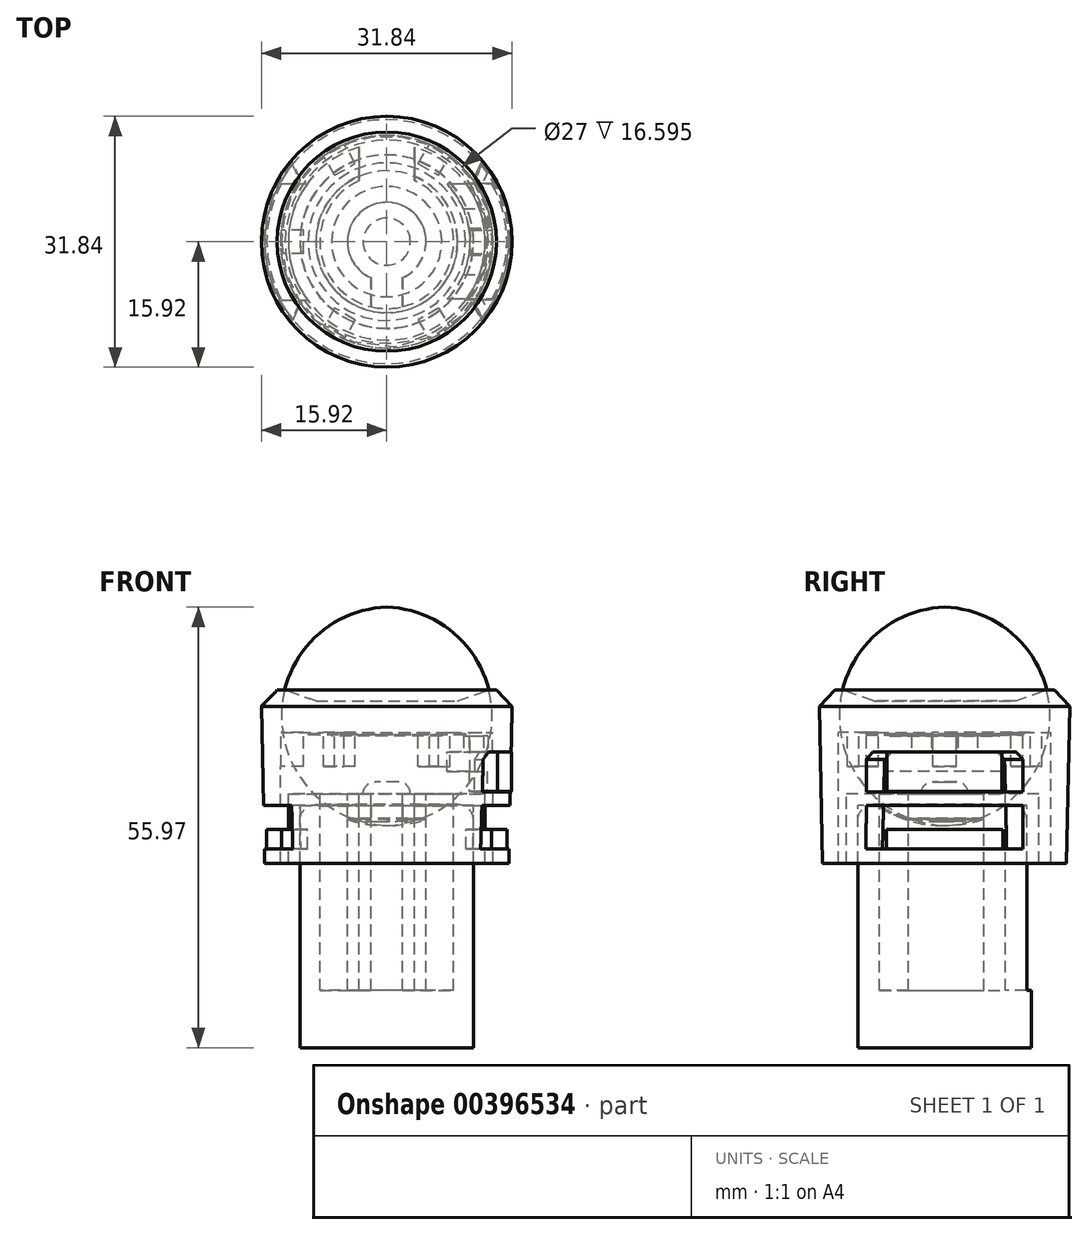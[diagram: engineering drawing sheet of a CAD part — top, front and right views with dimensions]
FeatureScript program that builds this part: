
annotation { "Feature Type Name" : "Feature", "Feature Type Description" : "" }
export const myFeature = defineFeature(function(context is Context, id is Id, definition is map)
    precondition{}
    {
        {
            var Q0;
            Q0=qCreatedBy(makeId("Front.planeOp"),FACE);
            var sketch = newSketch(context, id + "F0", { "sketchPlane" : qUnion([Q0])});
            skLineSegment(sketch, "E0", {"start": v(0, -0.44) * mm, "end": v(12.5, -0.44) * mm});
            skLineSegment(sketch, "E1", {"start": v(12.5, -0.44) * mm, "end": v(12.5, -9.24) * mm});
            skLineSegment(sketch, "E2", {"start": v(12.5, -9.24) * mm, "end": v(11, -9.24) * mm});
            skLineSegment(sketch, "E3", {"start": v(11, -9.24) * mm, "end": v(11, -1.94) * mm});
            skLineSegment(sketch, "E4", {"start": v(11, -1.94) * mm, "end": v(8.5, -1.94) * mm});
            skLineSegment(sketch, "E5.trimOffspring", {"start": v(0, -0.44) * mm, "end": v(0, -3.94) * mm, "construction": true});
            skLineSegment(sketch, "E6", {"start": v(0, -0.44) * mm, "end": v(0, -3.94) * mm});
            skPoint(sketch, "E7.start.orphan", {"position": v(0, 38.98) * mm});
            skFitSpline(sketch, "E8", {"points": [v(8.5, -1.94) * mm, v(4.82, -3.6) * mm, v(0, -3.94) * mm], "startDerivative": vector(-6.37, -4.3) * mm, "endDerivative": vector(-9.55, 0.19) * mm});
            skSolve(sketch);
        }
        {
            var Q0;
            Q0=qCreatedBy(makeId("Front.planeOp"),FACE);
            var sketch = newSketch(context, id + "F1", { "sketchPlane" : qUnion([Q0])});
            skLineSegment(sketch, "E9", {"start": v(0, 3.78) * mm, "end": v(0, -25.53) * mm, "construction": true});
            skLineSegment(sketch, "E10", {"start": v(11.03, -1.82) * mm, "end": v(11.03, -32.69) * mm});
            skLineSegment(sketch, "E11", {"start": v(11.03, -1.82) * mm, "end": v(8.62, -1.82) * mm});
            skLineSegment(sketch, "E12", {"start": v(0, -4.45) * mm, "end": v(0, -32.69) * mm});
            skArc(sketch, "E13", {"start": v(0, -4.45) * mm, "mid": v(4.53, -3.85) * mm, "end": v(8.62, -1.82) * mm});
            skLineSegment(sketch, "E14", {"start": v(0, -32.69) * mm, "end": v(11.03, -32.69) * mm});
            skSolve(sketch);
        }
        {
            var Q0;
            Q0=makeQuery(id+"F1.imprint","IMPRINT",FACE,{"disambiguationData":[TD([[makeQuery(id+"F1.imprint","IMPRINT",EDGE,{"derivedFrom":sQuery(id+"F1.wireOp",EDGE,"E10")}),-1.0]])]});
            var Q1;
            Q1=sQuery(id+"F1.wireOp",EDGE,"E12");
            revolve(context, id + "F2", {"entities" : qUnion([Q0]), "axis" : qUnion([Q1]), "revolveType" : RevolveType.FULL});
        }
        {
            var Q0;
            Q0=makeQuery(id+"F2.opRevolve","SWEPT_EDGE",EDGE,{"disambiguationData":[OSD([sQuery(id+"F1.wireOp",EDGE,"E10"),sQuery(id+"F1.wireOp",EDGE,"E11")])]});
            fillet(context, id + "F3", {"entities" : qUnion([Q0]), "radius" : 2 * mm, "tangentPropagation" : true, "allowEdgeOverflow" : false});
        }
        {
            var Q0;
            Q0=makeQuery(id+"F2.opRevolve","SWEPT_EDGE",EDGE,{"disambiguationData":[OSD([sQuery(id+"F1.wireOp",EDGE,"E11"),sQuery(id+"F1.wireOp",EDGE,"E13")])]});
            fillet(context, id + "F4", {"entities" : qUnion([Q0]), "radius" : 2 * mm, "tangentPropagation" : true, "allowEdgeOverflow" : false});
        }
        {
            var Q0;
            Q0 = qSketchRegion(id + "F0", true);
            var Q1;
            Q1=sQuery(id+"F0.wireOp",EDGE,"E6");
            revolve(context, id + "F5", {"entities" : qUnion([Q0]), "axis" : qUnion([Q1]), "revolveType" : RevolveType.FULL});
        }
        {
            var Q0;
            Q0=makeQuery(id+"F5.opRevolve","SWEPT_FACE",FACE,{"disambiguationData":[OSD([sQuery(id+"F0.wireOp",EDGE,"E0")])]});
            var sketch = newSketch(context, id + "F6", { "sketchPlane" : qUnion([Q0])});
            skArc(sketch, "E15", {"start": v(2, -4.58) * mm, "mid": v(0, 5) * mm, "end": v(-2, -4.58) * mm});
            skArc(sketch, "E16", {"start": v(2, -8.26) * mm, "mid": v(0, 8.5) * mm, "end": v(-2, -8.26) * mm});
            skLineSegment(sketch, "E17", {"start": v(0, 12.95) * mm, "end": v(0, -13.26) * mm, "construction": true});
            skLineSegment(sketch, "E18", {"start": v(2, -4.58) * mm, "end": v(2, -8.26) * mm});
            skLineSegment(sketch, "E19", {"start": v(-2, -4.58) * mm, "end": v(-2, -8.26) * mm});
            skSolve(sketch);
        }
        {
            var Q0;
            Q0=makeQuery(id+"F6.imprint","IMPRINT",FACE,{"disambiguationData":[TD([[makeQuery(id+"F6.imprint","IMPRINT",EDGE,{"derivedFrom":sQuery(id+"F6.wireOp",EDGE,"E15")}),-1.0]])]});
            extrude(context, id + "F7", {"entities" : qUnion([Q0]), "operationType" : NewBodyOperationType.REMOVE, "oppositeDirection" : true, "depth" : 25 * mm});
        }
        {
            var Q0;
            Q0=makeQuery(id+"F5.opRevolve","SWEPT_FACE",FACE,{"disambiguationData":[OSD([sQuery(id+"F0.wireOp",EDGE,"E0")])]});
            var sketch = newSketch(context, id + "F8", { "sketchPlane" : qUnion([Q0])});
            skLineSegment(sketch, "E20", {"start": v(0, 27.7) * mm, "end": v(0, -25.88) * mm, "construction": true});
            skLineSegment(sketch, "E21.bottom", {"start": v(-3.5, 14) * mm, "end": v(3.5, 14) * mm});
            skLineSegment(sketch, "E21.top", {"start": v(-3.5, 6.54) * mm, "end": v(3.5, 6.54) * mm});
            skLineSegment(sketch, "E21.left", {"start": v(-3.5, 14) * mm, "end": v(-3.5, 6.54) * mm});
            skLineSegment(sketch, "E21.right", {"start": v(3.5, 14) * mm, "end": v(3.5, 6.54) * mm});
            skSolve(sketch);
        }
        {
            var Q0;
            Q0 = qSketchRegion(id + "F8", true);
            extrude(context, id + "F9", {"entities" : qUnion([Q0]), "operationType" : NewBodyOperationType.REMOVE, "oppositeDirection" : true, "depth" : 25 * mm});
        }
        {
            var Q0;
            Q0=makeQuery(id+"F5.opRevolve","SWEPT_FACE",FACE,{"disambiguationData":[OSD([sQuery(id+"F0.wireOp",EDGE,"E0")])]});
            var sketch = newSketch(context, id + "F10", { "sketchPlane" : qUnion([Q0])});
            skCircle(sketch, "E22", {"center": v(0, 0) * mm, "radius": 3 * mm});
            skSolve(sketch);
        }
        {
            var Q0;
            Q0 = qSketchRegion(id + "F10", true);
            extrude(context, id + "F11", {"entities" : qUnion([Q0]), "operationType" : NewBodyOperationType.ADD, "depth" : 1.5 * mm});
        }
        {
            var Q0;
            Q0=makeQuery(id+"F11.opExtrude","CAP_EDGE",EDGE,{"disambiguationData":[OSD([sQuery(id+"F10.wireOp",EDGE,"E22")])],"isStart":false});
            fillet(context, id + "F12", {"entities" : qUnion([Q0]), "radius" : 1.5 * mm, "tangentPropagation" : true, "allowEdgeOverflow" : false});
        }
        {
            var Q0;
            Q0=makeQuery(id+"F5.opRevolve","SWEPT_FACE",FACE,{"disambiguationData":[OSD([sQuery(id+"F0.wireOp",EDGE,"E0")])]});
            var sketch = newSketch(context, id + "F13", { "sketchPlane" : qUnion([Q0])});
            skCircle(sketch, "E23", {"center": v(0, 0) * mm, "radius": 4 * mm});
            skCircle(sketch, "E24", {"center": v(0, 0) * mm, "radius": 9 * mm});
            skSolve(sketch);
        }
        {
            var Q0;
            Q0 = qSketchRegion(id + "F13", true);
            extrude(context, id + "F14", {"entities" : qUnion([Q0]), "depth" : 3.5 * mm});
        }
        {
            var Q0;
            Q0=makeQuery(id+"F14.opExtrude","CAP_FACE",FACE,{"disambiguationData":[OSD([sQuery(id+"F13.wireOp",EDGE,"E23"),sQuery(id+"F13.wireOp",EDGE,"E24")])],"isStart":false});
            var sketch = newSketch(context, id + "F15", { "sketchPlane" : qUnion([Q0])});
            skLineSegment(sketch, "E25", {"start": v(0, 4.46) * mm, "end": v(0, -5.35) * mm, "construction": true});
            skCircle(sketch, "E26", {"center": v(0, 0) * mm, "radius": 9.15 * mm});
            skSolve(sketch);
        }
        {
            var Q0;
            Q0 = qSketchRegion(id + "F15", true);
            extrude(context, id + "F16", {"entities" : qUnion([Q0]), "depth" : 1.27 * mm});
        }
        {
            var Q0;
            Q0=makeQuery(id+"F16.opExtrude","CAP_FACE",FACE,{"disambiguationData":[OSD([sQuery(id+"F15.wireOp",EDGE,"E26")])],"isStart":true});
            var sketch = newSketch(context, id + "F17", { "sketchPlane" : qUnion([Q0])});
            skLineSegment(sketch, "E27", {"start": v(0, 3.74) * mm, "end": v(0, -4.46) * mm, "construction": true});
            skLineSegment(sketch, "E28.bottom", {"start": v(-2.25, 2.25) * mm, "end": v(2.25, 2.25) * mm});
            skLineSegment(sketch, "E28.top", {"start": v(-2.25, -2.25) * mm, "end": v(2.25, -2.25) * mm});
            skLineSegment(sketch, "E28.left", {"start": v(-2.25, 2.25) * mm, "end": v(-2.25, -2.25) * mm});
            skLineSegment(sketch, "E28.right", {"start": v(2.25, 2.25) * mm, "end": v(2.25, -2.25) * mm});
            skSolve(sketch);
        }
        {
            var Q0;
            Q0 = qSketchRegion(id + "F17", true);
            extrude(context, id + "F18", {"entities" : qUnion([Q0]), "operationType" : NewBodyOperationType.ADD, "depth" : 0.25 * mm});
        }
        {
            var Q0;
            Q0=makeQuery(id+"F18.opExtrude","CAP_FACE",FACE,{"disambiguationData":[OSD([sQuery(id+"F17.wireOp",EDGE,"E28.bottom"),sQuery(id+"F17.wireOp",EDGE,"E28.top"),sQuery(id+"F17.wireOp",EDGE,"E28.left"),sQuery(id+"F17.wireOp",EDGE,"E28.right")])],"isStart":false});
            var sketch = newSketch(context, id + "F19", { "sketchPlane" : qUnion([Q0])});
            skCircle(sketch, "E29", {"center": v(0, 0) * mm, "radius": 1.75 * mm});
            skSolve(sketch);
        }
        {
            var Q0;
            Q0 = qSketchRegion(id + "F19", true);
            extrude(context, id + "F20", {"entities" : qUnion([Q0]), "operationType" : NewBodyOperationType.ADD, "depth" : 0.25 * mm});
        }
        {
            var Q0;
            Q0=makeQuery(id+"F16.opExtrude","CAP_FACE",FACE,{"disambiguationData":[OSD([sQuery(id+"F15.wireOp",EDGE,"E26")])],"isStart":false});
            var sketch = newSketch(context, id + "F21", { "sketchPlane" : qUnion([Q0])});
            skLineSegment(sketch, "E30", {"start": v(0, 7.63) * mm, "end": v(0, -7.56) * mm, "construction": true});
            skLineSegment(sketch, "E31", {"start": v(-7.85, 0) * mm, "end": v(8.99, 0) * mm, "construction": true});
            skLineSegment(sketch, "E32.bottom", {"start": v(-6.75, 4.5) * mm, "end": v(6.75, 4.5) * mm});
            skLineSegment(sketch, "E32.top", {"start": v(-6.75, -4.5) * mm, "end": v(6.75, -4.5) * mm});
            skLineSegment(sketch, "E32.left", {"start": v(-6.75, 4.5) * mm, "end": v(-6.75, -4.5) * mm});
            skLineSegment(sketch, "E32.right", {"start": v(6.75, 4.5) * mm, "end": v(6.75, -4.5) * mm});
            skSolve(sketch);
        }
        {
            var Q0;
            Q0 = qSketchRegion(id + "F21", true);
            extrude(context, id + "F22", {"entities" : qUnion([Q0]), "operationType" : NewBodyOperationType.ADD, "depth" : 2.6 * mm});
        }
        {
            var Q0;
            Q0=makeQuery(id+"F22.opExtrude","CAP_EDGE",EDGE,{"disambiguationData":[OSD([sQuery(id+"F21.wireOp",EDGE,"E32.left")])],"isStart":false});
            var Q1;
            Q1=makeQuery(id+"F22.opExtrude","CAP_EDGE",EDGE,{"disambiguationData":[OSD([sQuery(id+"F21.wireOp",EDGE,"E32.right")])],"isStart":false});
            chamfer(context, id + "F23", {"entities" : qUnion([Q0, Q1]), "width" : 0.5 * mm, "tangentPropagation" : true});
        }
        {
            var Q0;
            Q0=makeQuery(id+"F22.opExtrude","SWEPT_FACE",FACE,{"disambiguationData":[OSD([sQuery(id+"F21.wireOp",EDGE,"E32.top")])]});
            var sketch = newSketch(context, id + "F24", { "sketchPlane" : qUnion([Q0])});
            skLineSegment(sketch, "E33.bottom", {"start": v(-6.25, 4.33) * mm, "end": v(6.25, 4.33) * mm});
            skLineSegment(sketch, "E33.top", {"start": v(-6.25, 6.43) * mm, "end": v(6.25, 6.43) * mm});
            skLineSegment(sketch, "E33.left", {"start": v(-6.25, 4.33) * mm, "end": v(-6.25, 6.43) * mm});
            skLineSegment(sketch, "E33.right", {"start": v(6.25, 4.33) * mm, "end": v(6.25, 6.43) * mm});
            skSolve(sketch);
        }
        {
            var Q0;
            Q0 = qSketchRegion(id + "F24", true);
            extrude(context, id + "F25", {"entities" : qUnion([Q0]), "operationType" : NewBodyOperationType.REMOVE, "oppositeDirection" : true, "depth" : 17.3 * mm});
        }
        {
            var Q0;
            Q0=makeQuery(id+"F25.boolean.opBoolean","COPY",EDGE,{"derivedFrom":makeQuery(id+"F25.opExtrude","SWEPT_EDGE",EDGE,{"disambiguationData":[OSD([sQuery(id+"F24.wireOp",EDGE,"E33.top"),sQuery(id+"F24.wireOp",EDGE,"E33.right")])]})});
            var Q1;
            Q1=makeQuery(id+"F25.boolean.opBoolean","COPY",EDGE,{"derivedFrom":makeQuery(id+"F25.opExtrude","SWEPT_EDGE",EDGE,{"disambiguationData":[OSD([sQuery(id+"F24.wireOp",EDGE,"E33.top"),sQuery(id+"F24.wireOp",EDGE,"E33.left")])]})});
            chamfer(context, id + "F26", {"entities" : qUnion([Q0, Q1]), "width" : 0.25 * mm, "tangentPropagation" : true});
        }
        {
            var Q0;
            Q0=makeQuery(id+"F22.opExtrude","CAP_FACE",FACE,{"disambiguationData":[OSD([sQuery(id+"F21.wireOp",EDGE,"E32.bottom"),sQuery(id+"F21.wireOp",EDGE,"E32.top"),sQuery(id+"F21.wireOp",EDGE,"E32.left"),sQuery(id+"F21.wireOp",EDGE,"E32.right")])],"isStart":false});
            var sketch = newSketch(context, id + "F27", { "sketchPlane" : qUnion([Q0])});
            skCircle(sketch, "E34", {"center": v(0, 0) * mm, "radius": 7 * mm});
            skSolve(sketch);
        }
        {
            var Q0;
            Q0 = qSketchRegion(id + "F27", true);
            extrude(context, id + "F28", {"entities" : qUnion([Q0]), "depth" : 0.13 * mm});
        }
        {
            var Q0;
            Q0=makeQuery(id+"F28.opExtrude","CAP_FACE",FACE,{"disambiguationData":[OSD([sQuery(id+"F27.wireOp",EDGE,"E34")])],"isStart":false});
            var sketch = newSketch(context, id + "F29", { "sketchPlane" : qUnion([Q0])});
            skCircle(sketch, "E35", {"center": v(0, 0) * mm, "radius": 10 * mm});
            skSolve(sketch);
        }
        {
            var Q0;
            Q0 = qSketchRegion(id + "F29", true);
            extrude(context, id + "F30", {"entities" : qUnion([Q0]), "operationType" : NewBodyOperationType.ADD, "depth" : 0.1 * mm});
        }
        {
            var Q0;
            Q0=makeQuery(id+"F16.opExtrude","CAP_FACE",FACE,{"disambiguationData":[OSD([sQuery(id+"F15.wireOp",EDGE,"E26")])],"isStart":true});
            var sketch = newSketch(context, id + "F31", { "sketchPlane" : qUnion([Q0])});
            skLineSegment(sketch, "E36", {"start": v(-8.27, 0) * mm, "end": v(8.46, 0) * mm, "construction": true});
            skPoint(sketch, "E36.endSnap0", {"position": v(2.25, 0) * mm});
            skLineSegment(sketch, "E37.bottom", {"start": v(8.98, 1.75) * mm, "end": v(5.43, 1.75) * mm});
            skLineSegment(sketch, "E37.top", {"start": v(8.98, -1.75) * mm, "end": v(5.43, -1.75) * mm});
            skLineSegment(sketch, "E37.left", {"start": v(8.98, 1.75) * mm, "end": v(8.98, -1.75) * mm});
            skLineSegment(sketch, "E37.right", {"start": v(5.43, 1.75) * mm, "end": v(5.43, -1.75) * mm});
            skSolve(sketch);
        }
        {
            var Q0;
            Q0 = qSketchRegion(id + "F31", true);
            extrude(context, id + "F32", {"entities" : qUnion([Q0]), "operationType" : NewBodyOperationType.ADD, "depth" : 1.35 * mm});
        }
        {
            var Q0;
            Q0=makeQuery(id+"F32.opExtrude","SWEPT_FACE",FACE,{"disambiguationData":[OSD([sQuery(id+"F31.wireOp",EDGE,"E37.left")])]});
            var sketch = newSketch(context, id + "F33", { "sketchPlane" : qUnion([Q0])});
            skLineSegment(sketch, "E38", {"start": v(0, 2.91) * mm, "end": v(0, 0.9) * mm, "construction": true});
            skLineSegment(sketch, "E39.bottom", {"start": v(-0.83, 2.89) * mm, "end": v(0.87, 2.89) * mm});
            skLineSegment(sketch, "E39.top", {"start": v(-0.83, 1.89) * mm, "end": v(0.87, 1.89) * mm});
            skLineSegment(sketch, "E39.left", {"start": v(-0.83, 2.89) * mm, "end": v(-0.83, 1.89) * mm});
            skLineSegment(sketch, "E39.right", {"start": v(0.87, 2.89) * mm, "end": v(0.87, 1.89) * mm});
            skLineSegment(sketch, "E40", {"start": v(-1.75, 2.39) * mm, "end": v(2.35, 2.39) * mm, "construction": true});
            skPoint(sketch, "E40.endSnap0", {"position": v(1.75, 2.39) * mm});
            skSolve(sketch);
        }
        {
            var Q0;
            Q0 = qSketchRegion(id + "F33", true);
            extrude(context, id + "F34", {"entities" : qUnion([Q0]), "operationType" : NewBodyOperationType.ADD, "depth" : 0.1 * mm});
        }
        {
            var Q0;
            Q0=qCreatedBy(makeId("Front.planeOp"),FACE);
            var sketch = newSketch(context, id + "F35", { "sketchPlane" : qUnion([Q0])});
            skLineSegment(sketch, "E41", {"start": v(0, 13.97) * mm, "end": v(0, -10.82) * mm, "construction": true});
            skLineSegment(sketch, "E42", {"start": v(-13.5, 2.98) * mm, "end": v(-13.5, -9.27) * mm});
            skLineSegment(sketch, "E43", {"start": v(-13.5, -9.27) * mm, "end": v(-15.5, -9.27) * mm});
            skLineSegment(sketch, "E44", {"start": v(-15.97, 12.72) * mm, "end": v(0, 12.72) * mm});
            skLineSegment(sketch, "E45", {"start": v(-12, -3.77) * mm, "end": v(-12, -9.75) * mm, "construction": true});
            skLineSegment(sketch, "E46", {"start": v(0, 7.32) * mm, "end": v(0, 12.72) * mm});
            skLineSegment(sketch, "E47", {"start": v(0, 7.32) * mm, "end": v(-13.5, 7.32) * mm});
            skLineSegment(sketch, "E48", {"start": v(-13.5, 7.32) * mm, "end": v(-13.5, 2.98) * mm});
            skLineSegment(sketch, "E49", {"start": v(-15.5, -9.27) * mm, "end": v(-15.97, 12.72) * mm});
            skSolve(sketch);
        }
        {
            var Q0;
            Q0 = qSketchRegion(id + "F35", true);
            var Q1;
            Q1=sQuery(id+"F35.wireOp",EDGE,"E41");
            revolve(context, id + "F36", {"entities" : qUnion([Q0]), "axis" : qUnion([Q1]), "revolveType" : RevolveType.FULL});
        }
        {
            var Q0;
            Q0=makeQuery(id+"F36.opRevolve","SWEPT_EDGE",EDGE,{"disambiguationData":[OSD([sQuery(id+"F35.wireOp",EDGE,"E44"),sQuery(id+"F35.wireOp",EDGE,"d65c96e9-5ec0-4ce5-985c-a884ea4e2c14")])]});
            chamfer(context, id + "F37", {"entities" : qUnion([Q0]), "width" : 2 * mm, "tangentPropagation" : true});
        }
        {
            var Q0;
            Q0=qCreatedBy(makeId("Front.planeOp"),FACE);
            var sketch = newSketch(context, id + "F38", { "sketchPlane" : qUnion([Q0])});
            skLineSegment(sketch, "E50", {"start": v(0, 14.74) * mm, "end": v(0, -8.47) * mm, "construction": true});
            skLineSegment(sketch, "E51", {"start": v(0, 13.12) * mm, "end": v(0, 11.34) * mm});
            skLineSegment(sketch, "E52", {"start": v(0, 11.34) * mm, "end": v(-9, 11.34) * mm});
            skLineSegment(sketch, "E53", {"start": v(-9, 11.34) * mm, "end": v(-14, 13.12) * mm});
            skLineSegment(sketch, "E54", {"start": v(-14, 13.12) * mm, "end": v(0, 13.12) * mm});
            skSolve(sketch);
        }
        {
            var Q0;
            Q0 = qSketchRegion(id + "F38", true);
            var Q1;
            Q1=sQuery(id+"F38.wireOp",EDGE,"E50");
            revolve(context, id + "F39", {"operationType" : NewBodyOperationType.REMOVE, "entities" : qUnion([Q0]), "axis" : qUnion([Q1]), "revolveType" : RevolveType.FULL, "oppositeDirection" : true});
        }
        {
            var Q0;
            Q0=makeQuery(id+"F36.opRevolve","SWEPT_FACE",FACE,{"disambiguationData":[OSD([sQuery(id+"F35.wireOp",EDGE,"E47")])]});
            var sketch = newSketch(context, id + "F40", { "sketchPlane" : qUnion([Q0])});
            skLineSegment(sketch, "E55", {"start": v(0, 14.03) * mm, "end": v(0, -14.75) * mm, "construction": true});
            skLineSegment(sketch, "E56", {"start": v(-18.67, 0) * mm, "end": v(14.75, 0) * mm, "construction": true});
            skArc(sketch, "E57", {"start": v(-13.42, 1.5) * mm, "mid": v(-13.5, 0) * mm, "end": v(-13.42, -1.5) * mm});
            skLineSegment(sketch, "E58", {"start": v(-10.6, 1.5) * mm, "end": v(-10.6, -1.5) * mm});
            skLineSegment(sketch, "E59", {"start": v(-10.6, 1.5) * mm, "end": v(-13.42, 1.5) * mm});
            skLineSegment(sketch, "E60", {"start": v(-10.6, -1.5) * mm, "end": v(-13.42, -1.5) * mm});
            skLineSegment(sketch, "E61.1.0", {"start": v(-4, 9.93) * mm, "end": v(-5.4, 12.37) * mm});
            skLineSegment(sketch, "E61.1.1", {"start": v(-4, 9.93) * mm, "end": v(-6.6, 8.43) * mm});
            skLineSegment(sketch, "E61.1.2", {"start": v(-6.6, 8.43) * mm, "end": v(-8, 10.87) * mm});
            skLineSegment(sketch, "E61.2.0", {"start": v(6.6, 8.43) * mm, "end": v(8, 10.87) * mm});
            skLineSegment(sketch, "E61.2.1", {"start": v(6.6, 8.43) * mm, "end": v(4, 9.93) * mm});
            skLineSegment(sketch, "E61.2.2", {"start": v(4, 9.93) * mm, "end": v(5.4, 12.37) * mm});
            skLineSegment(sketch, "E61.3.0", {"start": v(10.6, -1.5) * mm, "end": v(13.42, -1.5) * mm});
            skLineSegment(sketch, "E61.3.1", {"start": v(10.6, -1.5) * mm, "end": v(10.6, 1.5) * mm});
            skLineSegment(sketch, "E61.3.2", {"start": v(10.6, 1.5) * mm, "end": v(13.42, 1.5) * mm});
            skLineSegment(sketch, "E61.4.0", {"start": v(4, -9.93) * mm, "end": v(5.4, -12.37) * mm});
            skLineSegment(sketch, "E61.4.1", {"start": v(4, -9.93) * mm, "end": v(6.6, -8.43) * mm});
            skLineSegment(sketch, "E61.4.2", {"start": v(6.6, -8.43) * mm, "end": v(8, -10.87) * mm});
            skLineSegment(sketch, "E61.5.0", {"start": v(-6.6, -8.43) * mm, "end": v(-8, -10.87) * mm});
            skLineSegment(sketch, "E61.5.1", {"start": v(-6.6, -8.43) * mm, "end": v(-4, -9.93) * mm});
            skLineSegment(sketch, "E61.5.2", {"start": v(-4, -9.93) * mm, "end": v(-5.4, -12.37) * mm});
            skLineSegment(sketch, "E61.anchor1", {"start": v(0, 0) * mm, "end": v(-13.42, 1.5) * mm, "construction": true});
            skLineSegment(sketch, "E61.anchor2", {"start": v(0, 0) * mm, "end": v(-8, -10.87) * mm, "construction": true});
            skArc(sketch, "E62.trimOffspring", {"start": v(-5.4, 12.37) * mm, "mid": v(-6.75, 11.7) * mm, "end": v(-8, 10.87) * mm});
            skArc(sketch, "E63.trimOffspring", {"start": v(8, 10.87) * mm, "mid": v(6.75, 11.7) * mm, "end": v(5.4, 12.37) * mm});
            skArc(sketch, "E64.trimOffspring", {"start": v(13.42, -1.5) * mm, "mid": v(13.5, 0) * mm, "end": v(13.42, 1.5) * mm});
            skArc(sketch, "E65.trimOffspring", {"start": v(5.4, -12.37) * mm, "mid": v(6.75, -11.7) * mm, "end": v(8, -10.87) * mm});
            skArc(sketch, "E66.trimOffspring", {"start": v(-8, -10.87) * mm, "mid": v(-6.75, -11.7) * mm, "end": v(-5.4, -12.37) * mm});
            skSolve(sketch);
        }
        {
            var Q0;
            Q0=makeQuery(id+"F40.imprint","IMPRINT",FACE,{"disambiguationData":[TD([[makeQuery(id+"F40.imprint","IMPRINT",EDGE,{"derivedFrom":sQuery(id+"F40.wireOp",EDGE,"E57")}),-1.0]])]});
            var Q1;
            Q1=makeQuery(id+"F40.imprint","IMPRINT",FACE,{"disambiguationData":[TD([[makeQuery(id+"F40.imprint","IMPRINT",EDGE,{"derivedFrom":sQuery(id+"F40.wireOp",EDGE,"E61.2.0")}),1.0]])]});
            var Q2;
            Q2=makeQuery(id+"F40.imprint","IMPRINT",FACE,{"disambiguationData":[TD([[makeQuery(id+"F40.imprint","IMPRINT",EDGE,{"derivedFrom":sQuery(id+"F40.wireOp",EDGE,"E61.3.0")}),1.0]])]});
            var Q3;
            Q3=makeQuery(id+"F40.imprint","IMPRINT",FACE,{"disambiguationData":[TD([[makeQuery(id+"F40.imprint","IMPRINT",EDGE,{"derivedFrom":sQuery(id+"F40.wireOp",EDGE,"E61.4.0")}),1.0]])]});
            var Q4;
            Q4=makeQuery(id+"F40.imprint","IMPRINT",FACE,{"disambiguationData":[TD([[makeQuery(id+"F40.imprint","IMPRINT",EDGE,{"derivedFrom":sQuery(id+"F40.wireOp",EDGE,"E61.5.0")}),1.0]])]});
            var Q5;
            Q5=makeQuery(id+"F40.imprint","IMPRINT",FACE,{"disambiguationData":[TD([[makeQuery(id+"F40.imprint","IMPRINT",EDGE,{"derivedFrom":sQuery(id+"F40.wireOp",EDGE,"E61.1.0")}),1.0]])]});
            extrude(context, id + "F41", {"entities" : qUnion([Q0, Q1, Q2, Q3, Q4, Q5]), "operationType" : NewBodyOperationType.ADD, "depth" : 4.3 * mm});
        }
        {
            var Q0;
            Q0=makeQuery(id+"F41.opExtrude","CAP_FACE",FACE,{"disambiguationData":[OSD([sQuery(id+"F40.wireOp",EDGE,"E61.3.0"),sQuery(id+"F40.wireOp",EDGE,"E61.3.1"),sQuery(id+"F40.wireOp",EDGE,"E61.3.2"),sQuery(id+"F40.wireOp",EDGE,"E64.trimOffspring")])],"isStart":false});
            var sketch = newSketch(context, id + "F42", { "sketchPlane" : qUnion([Q0])});
            skLineSegment(sketch, "E67", {"start": v(-17, 0) * mm, "end": v(23.35, 0) * mm, "construction": true});
            skArc(sketch, "E68", {"start": v(7.5, -7.5) * mm, "mid": v(10.6, 0) * mm, "end": v(7.5, 7.5) * mm});
            skLineSegment(sketch, "E69", {"start": v(20.33, 7.5) * mm, "end": v(20.33, -7.5) * mm});
            skLineSegment(sketch, "E70", {"start": v(20.33, 7.5) * mm, "end": v(7.5, 7.5) * mm});
            skLineSegment(sketch, "E71", {"start": v(20.33, -7.5) * mm, "end": v(7.5, -7.5) * mm});
            skSolve(sketch);
        }
        {
            var Q0;
            Q0 = qSketchRegion(id + "F42", true);
            extrude(context, id + "F43", {"entities" : qUnion([Q0]), "operationType" : NewBodyOperationType.REMOVE, "oppositeDirection" : true, "depth" : 1.87 * mm, "hasSecondDirection" : true, "secondDirectionOppositeDirection" : false, "secondDirectionDepth" : 3.2 * mm});
        }
        {
            var Q0;
            Q0=makeQuery(id+"F43.boolean.opBoolean","COPY",FACE,{"derivedFrom":makeQuery(id+"F43.opExtrude","CAP_FACE",FACE,{"disambiguationData":[OSD([sQuery(id+"F42.wireOp",EDGE,"E68"),sQuery(id+"F42.wireOp",EDGE,"E69"),sQuery(id+"F42.wireOp",EDGE,"E70"),sQuery(id+"F42.wireOp",EDGE,"E71")])],"isStart":false})});
            var sketch = newSketch(context, id + "F44", { "sketchPlane" : qUnion([Q0])});
            skLineSegment(sketch, "E72", {"start": v(0, 0) * mm, "end": v(15.87, 0) * mm});
            skPoint(sketch, "E72.endSnap0", {"position": v(15.8, 0) * mm});
            skArc(sketch, "E73", {"start": v(14.09, -7.3) * mm, "mid": v(15.87, 0) * mm, "end": v(14.09, 7.3) * mm});
            skPoint(sketch, "E74.end.orphan", {"position": v(15.5, -7.4) * mm});
            skArc(sketch, "E75", {"start": v(7.69, -7.3) * mm, "mid": v(10.6, 0) * mm, "end": v(7.69, 7.3) * mm});
            skLineSegment(sketch, "E76", {"start": v(14.09, -7.3) * mm, "end": v(7.69, -7.3) * mm});
            skLineSegment(sketch, "E77", {"start": v(14.09, 7.3) * mm, "end": v(7.69, 7.3) * mm});
            skPoint(sketch, "E78.orphan", {"position": v(-6.1, 0) * mm});
            skPoint(sketch, "E79.orphan", {"position": v(26.21, 0) * mm});
            skSolve(sketch);
        }
        {
            var Q0;
            Q0 = qSketchRegion(id + "F44", true);
            extrude(context, id + "F45", {"entities" : qUnion([Q0]), "depth" : 5 * mm});
        }
        {
            var Q0;
            Q0 = qSketchRegion(id + "F44", true);
            extrude(context, id + "F46", {"entities" : qUnion([Q0]), "depth" : 5 * mm});
        }
        {
            var Q0;
            Q0=makeQuery(id+"F45.opExtrude","SWEPT_BODY",BODY,{"disambiguationData":[OSD([sQuery(id+"F44.wireOp",EDGE,"E73"),sQuery(id+"F44.wireOp",EDGE,"E75"),sQuery(id+"F44.wireOp",EDGE,"E76"),sQuery(id+"F44.wireOp",EDGE,"E77")])]});
            deleteBodies(context, id + "F47", {"entities" : qUnion([Q0])});
        }
        {
            var Q0;
            Q0=makeQuery(id+"F46.opExtrude","CAP_FACE",FACE,{"disambiguationData":[OSD([sQuery(id+"F44.wireOp",EDGE,"E73"),sQuery(id+"F44.wireOp",EDGE,"E75"),sQuery(id+"F44.wireOp",EDGE,"E76"),sQuery(id+"F44.wireOp",EDGE,"E77")])],"isStart":true});
            var sketch = newSketch(context, id + "F48", { "sketchPlane" : qUnion([Q0])});
            skLineSegment(sketch, "E80", {"start": v(-2.73, 0) * mm, "end": v(17.53, 0) * mm, "construction": true});
            skPoint(sketch, "E80.endSnap0", {"position": v(15.87, 0) * mm});
            skArc(sketch, "E81", {"start": v(12.89, 1.7) * mm, "mid": v(12.66, 2.96) * mm, "end": v(12.3, 4.2) * mm});
            skArc(sketch, "E82", {"start": v(9.73, -4.2) * mm, "mid": v(10.17, -2.97) * mm, "end": v(10.46, -1.7) * mm});
            skLineSegment(sketch, "E83", {"start": v(10.46, 1.7) * mm, "end": v(12.89, 1.7) * mm});
            skLineSegment(sketch, "E84", {"start": v(10.46, -1.7) * mm, "end": v(12.89, -1.7) * mm});
            skLineSegment(sketch, "E85", {"start": v(9.73, 4.2) * mm, "end": v(12.3, 4.2) * mm});
            skLineSegment(sketch, "E86", {"start": v(9.73, -4.2) * mm, "end": v(12.3, -4.2) * mm});
            skArc(sketch, "E87.trimOffspring", {"start": v(10.46, 1.7) * mm, "mid": v(10.17, 2.97) * mm, "end": v(9.73, 4.2) * mm});
            skArc(sketch, "E88.trimOffspring", {"start": v(12.3, -4.2) * mm, "mid": v(12.66, -2.96) * mm, "end": v(12.89, -1.7) * mm});
            skSolve(sketch);
        }
        {
            var Q0;
            Q0 = qSketchRegion(id + "F48", true);
            extrude(context, id + "F49", {"entities" : qUnion([Q0]), "operationType" : NewBodyOperationType.ADD, "depth" : 2 * mm});
        }
        {
            var Q0;
            Q0=makeQuery(id+"F46.opExtrude","CAP_FACE",FACE,{"disambiguationData":[OSD([sQuery(id+"F44.wireOp",EDGE,"E73"),sQuery(id+"F44.wireOp",EDGE,"E75"),sQuery(id+"F44.wireOp",EDGE,"E76"),sQuery(id+"F44.wireOp",EDGE,"E77")])],"isStart":false});
            var sketch = newSketch(context, id + "F50", { "sketchPlane" : qUnion([Q0])});
            skArc(sketch, "E89", {"start": v(7.69, -7.3) * mm, "mid": v(10.6, 0) * mm, "end": v(7.69, 7.3) * mm});
            skLineSegment(sketch, "E90", {"start": v(-7.31, 0) * mm, "end": v(18.85, 0) * mm, "construction": true});
            skPoint(sketch, "E90.endSnap0", {"position": v(15.87, 0) * mm});
            skArc(sketch, "E91", {"start": v(10.45, -7.3) * mm, "mid": v(12.75, 0) * mm, "end": v(10.45, 7.3) * mm});
            skPoint(sketch, "E92.MirrorCS.end.orphan", {"position": v(9.65, 7.3) * mm});
            skPoint(sketch, "E93.end.orphan", {"position": v(9.65, -7.3) * mm});
            skLineSegment(sketch, "E94", {"start": v(7.69, -7.3) * mm, "end": v(10.45, -7.3) * mm});
            skLineSegment(sketch, "E95", {"start": v(7.69, 7.3) * mm, "end": v(10.45, 7.3) * mm});
            skSolve(sketch);
        }
        {
            var Q0;
            Q0 = qSketchRegion(id + "F50", true);
            extrude(context, id + "F51", {"entities" : qUnion([Q0]), "operationType" : NewBodyOperationType.REMOVE, "oppositeDirection" : true, "depth" : 2.5 * mm});
        }
        {
            var Q0;
            Q0=makeQuery(id+"F5.opRevolve","SWEPT_FACE",FACE,{"disambiguationData":[OSD([sQuery(id+"F0.wireOp",EDGE,"E4")])]});
            var sketch = newSketch(context, id + "F52", { "sketchPlane" : qUnion([Q0])});
            skLineSegment(sketch, "E96", {"start": v(-6.96, 0) * mm, "end": v(23.93, 0) * mm, "construction": true});
            skArc(sketch, "E97", {"start": v(10.05, -7.5) * mm, "mid": v(12.54, 0) * mm, "end": v(10.05, 7.5) * mm});
            skLineSegment(sketch, "E98", {"start": v(18.52, 7.5) * mm, "end": v(18.52, -7.5) * mm});
            skLineSegment(sketch, "E99", {"start": v(18.52, 7.5) * mm, "end": v(10.05, 7.5) * mm});
            skLineSegment(sketch, "E100", {"start": v(18.52, -7.5) * mm, "end": v(10.05, -7.5) * mm});
            skLineSegment(sketch, "E101", {"start": v(0, -6.87) * mm, "end": v(0, 12.05) * mm, "construction": true});
            skPoint(sketch, "E101.endSnap0", {"position": v(0, 11) * mm});
            skArc(sketch, "E102.MirrorCS", {"start": v(-10.05, -7.5) * mm, "mid": v(-12.54, 0) * mm, "end": v(-10.05, 7.5) * mm});
            skLineSegment(sketch, "E103.MirrorCS", {"start": v(-18.52, -7.5) * mm, "end": v(-10.05, -7.5) * mm});
            skLineSegment(sketch, "E104.MirrorCS", {"start": v(-18.52, 7.5) * mm, "end": v(-18.52, -7.5) * mm});
            skLineSegment(sketch, "E105.MirrorCS", {"start": v(-18.52, 7.5) * mm, "end": v(-10.05, 7.5) * mm});
            skSolve(sketch);
        }
        {
            var Q0;
            Q0 = qSketchRegion(id + "F52", true);
            extrude(context, id + "F53", {"entities" : qUnion([Q0]), "operationType" : NewBodyOperationType.REMOVE, "depth" : 5.5 * mm});
        }
        {
            var Q0;
            Q0=makeQuery(id+"F53.boolean.opBoolean","COPY",FACE,{"derivedFrom":makeQuery(id+"F53.opExtrude","CAP_FACE",FACE,{"disambiguationData":[OSD([sQuery(id+"F52.wireOp",EDGE,"E97"),sQuery(id+"F52.wireOp",EDGE,"E98"),sQuery(id+"F52.wireOp",EDGE,"E99"),sQuery(id+"F52.wireOp",EDGE,"E100")])],"isStart":false})});
            var sketch = newSketch(context, id + "F54", { "sketchPlane" : qUnion([Q0])});
            skLineSegment(sketch, "E106", {"start": v(-4.46, 0) * mm, "end": v(22.33, 0) * mm, "construction": true});
            skPoint(sketch, "E106.endSnap0", {"position": v(13.5, 0) * mm});
            skArc(sketch, "E107", {"start": v(9.45, -7.4) * mm, "mid": v(12, 0) * mm, "end": v(9.45, 7.4) * mm});
            skArc(sketch, "E108", {"start": v(13.33, -7.4) * mm, "mid": v(15.25, 0) * mm, "end": v(13.33, 7.4) * mm});
            skLineSegment(sketch, "E109", {"start": v(0, 7.11) * mm, "end": v(0, -8.04) * mm, "construction": true});
            skLineSegment(sketch, "E110", {"start": v(13.33, 7.4) * mm, "end": v(9.45, 7.4) * mm});
            skLineSegment(sketch, "E111", {"start": v(13.33, -7.4) * mm, "end": v(9.45, -7.4) * mm});
            skPoint(sketch, "E112.orphan", {"position": v(15.82, -7.4) * mm});
            skArc(sketch, "E113.MirrorCS", {"start": v(-9.45, -7.4) * mm, "mid": v(-12, 0) * mm, "end": v(-9.45, 7.4) * mm});
            skLineSegment(sketch, "E114.MirrorCS", {"start": v(-13.33, 7.4) * mm, "end": v(-9.45, 7.4) * mm});
            skArc(sketch, "E115.MirrorCS", {"start": v(-13.33, -7.4) * mm, "mid": v(-15.25, 0) * mm, "end": v(-13.33, 7.4) * mm});
            skLineSegment(sketch, "E116.MirrorCS", {"start": v(-13.33, -7.4) * mm, "end": v(-9.45, -7.4) * mm});
            skSolve(sketch);
        }
        {
            var Q0;
            Q0 = qSketchRegion(id + "F54", true);
            extrude(context, id + "F55", {"entities" : qUnion([Q0]), "operationType" : NewBodyOperationType.ADD, "depth" : 2.5 * mm});
        }
        {
            var Q0;
            Q0=makeQuery(id+"F14.opExtrude","SWEPT_BODY",BODY,{"disambiguationData":[OSD([sQuery(id+"F13.wireOp",EDGE,"E23"),sQuery(id+"F13.wireOp",EDGE,"E24")])]});
            deleteBodies(context, id + "F56", {"entities" : qUnion([Q0])});
        }
        {
            var Q0;
            Q0=makeQuery(id+"F53.boolean.opBoolean","INTERSECT",EDGE,{"derivedFrom":[makeQuery(id+"F36.opRevolve","SWEPT_FACE",FACE,{"disambiguationData":[OSD([sQuery(id+"F35.wireOp",EDGE,"E49")])]}),makeQuery(id+"F53.opExtrude","SWEPT_FACE",FACE,{"disambiguationData":[OSD([sQuery(id+"F52.wireOp",EDGE,"E105.MirrorCS")])]})]});
            var Q1;
            Q1=makeQuery(id+"F53.boolean.opBoolean","INTERSECT",EDGE,{"derivedFrom":[makeQuery(id+"F36.opRevolve","SWEPT_FACE",FACE,{"disambiguationData":[OSD([sQuery(id+"F35.wireOp",EDGE,"E49")])]}),makeQuery(id+"F53.opExtrude","SWEPT_FACE",FACE,{"disambiguationData":[OSD([sQuery(id+"F52.wireOp",EDGE,"E103.MirrorCS")])]})]});
            chamfer(context, id + "F57", {"entities" : qUnion([Q0, Q1]), "width" : 1.5 * mm, "tangentPropagation" : true});
        }
        {
            var Q0;
            Q0=makeQuery(id+"F53.boolean.opBoolean","INTERSECT",EDGE,{"derivedFrom":[makeQuery(id+"F36.opRevolve","SWEPT_FACE",FACE,{"disambiguationData":[OSD([sQuery(id+"F35.wireOp",EDGE,"E49")])]}),makeQuery(id+"F53.opExtrude","SWEPT_FACE",FACE,{"disambiguationData":[OSD([sQuery(id+"F52.wireOp",EDGE,"E100")])]})]});
            var Q1;
            Q1=makeQuery(id+"F53.boolean.opBoolean","INTERSECT",EDGE,{"derivedFrom":[makeQuery(id+"F36.opRevolve","SWEPT_FACE",FACE,{"disambiguationData":[OSD([sQuery(id+"F35.wireOp",EDGE,"E49")])]}),makeQuery(id+"F53.opExtrude","SWEPT_FACE",FACE,{"disambiguationData":[OSD([sQuery(id+"F52.wireOp",EDGE,"E99")])]})]});
            chamfer(context, id + "F58", {"entities" : qUnion([Q0, Q1]), "width" : 1.5 * mm, "tangentPropagation" : true});
        }
        {
            var Q0;
            Q0=makeQuery(id+"F43.boolean.opBoolean","INTERSECT",EDGE,{"derivedFrom":[makeQuery(id+"F36.opRevolve","SWEPT_FACE",FACE,{"disambiguationData":[OSD([sQuery(id+"F35.wireOp",EDGE,"E49")])]}),makeQuery(id+"F43.opExtrude","SWEPT_FACE",FACE,{"disambiguationData":[OSD([sQuery(id+"F42.wireOp",EDGE,"E71")])]})]});
            var Q1;
            Q1=makeQuery(id+"F43.boolean.opBoolean","INTERSECT",EDGE,{"derivedFrom":[makeQuery(id+"F36.opRevolve","SWEPT_FACE",FACE,{"disambiguationData":[OSD([sQuery(id+"F35.wireOp",EDGE,"E49")])]}),makeQuery(id+"F43.opExtrude","SWEPT_FACE",FACE,{"disambiguationData":[OSD([sQuery(id+"F42.wireOp",EDGE,"E70")])]})]});
            chamfer(context, id + "F59", {"entities" : qUnion([Q0, Q1]), "width" : 1.5 * mm, "tangentPropagation" : true});
        }
        {
            var Q0;
            {var subQ0=sQuery(id+"F42.wireOp",EDGE,"E71");Q0=makeQuery(id+"F59.opChamfer","BLEND_EDGE",EDGE,{"blendedFrom":[makeQuery(id+"F43.boolean.opBoolean","INTERSECT",EDGE,{"derivedFrom":[makeQuery(id+"F36.opRevolve","SWEPT_FACE",FACE,{"disambiguationData":[OSD([sQuery(id+"F35.wireOp",EDGE,"E49")])]}),makeQuery(id+"F43.opExtrude","SWEPT_FACE",FACE,{"disambiguationData":[OSD([subQ0])]})]}),makeQuery(id+"F43.boolean.opBoolean","COPY",FACE,{"derivedFrom":makeQuery(id+"F43.opExtrude","CAP_FACE",FACE,{"disambiguationData":[OSD([sQuery(id+"F42.wireOp",EDGE,"E68"),sQuery(id+"F42.wireOp",EDGE,"E69"),sQuery(id+"F42.wireOp",EDGE,"E70"),subQ0])],"isStart":false})})],"blendedInto":[makeQuery(id+"F43.boolean.opBoolean","COPY",FACE,{"derivedFrom":makeQuery(id+"F43.opExtrude","CAP_FACE",FACE,{"disambiguationData":[OSD([sQuery(id+"F42.wireOp",EDGE,"E68"),sQuery(id+"F42.wireOp",EDGE,"E69"),sQuery(id+"F42.wireOp",EDGE,"E70"),subQ0])],"isStart":false})})]});}
            var Q1;
            {var subQ0=sQuery(id+"F42.wireOp",EDGE,"E70");Q1=makeQuery(id+"F59.opChamfer","BLEND_EDGE",EDGE,{"blendedFrom":[makeQuery(id+"F43.boolean.opBoolean","INTERSECT",EDGE,{"derivedFrom":[makeQuery(id+"F36.opRevolve","SWEPT_FACE",FACE,{"disambiguationData":[OSD([sQuery(id+"F35.wireOp",EDGE,"E49")])]}),makeQuery(id+"F43.opExtrude","SWEPT_FACE",FACE,{"disambiguationData":[OSD([subQ0])]})]}),makeQuery(id+"F43.boolean.opBoolean","COPY",FACE,{"derivedFrom":makeQuery(id+"F43.opExtrude","CAP_FACE",FACE,{"disambiguationData":[OSD([sQuery(id+"F42.wireOp",EDGE,"E68"),sQuery(id+"F42.wireOp",EDGE,"E69"),subQ0,sQuery(id+"F42.wireOp",EDGE,"E71")])],"isStart":false})})],"blendedInto":[makeQuery(id+"F43.boolean.opBoolean","COPY",FACE,{"derivedFrom":makeQuery(id+"F43.opExtrude","CAP_FACE",FACE,{"disambiguationData":[OSD([sQuery(id+"F42.wireOp",EDGE,"E68"),sQuery(id+"F42.wireOp",EDGE,"E69"),subQ0,sQuery(id+"F42.wireOp",EDGE,"E71")])],"isStart":false})})]});}
            chamfer(context, id + "F60", {"entities" : qUnion([Q0, Q1]), "width" : 1 * mm, "tangentPropagation" : true});
        }
    });
